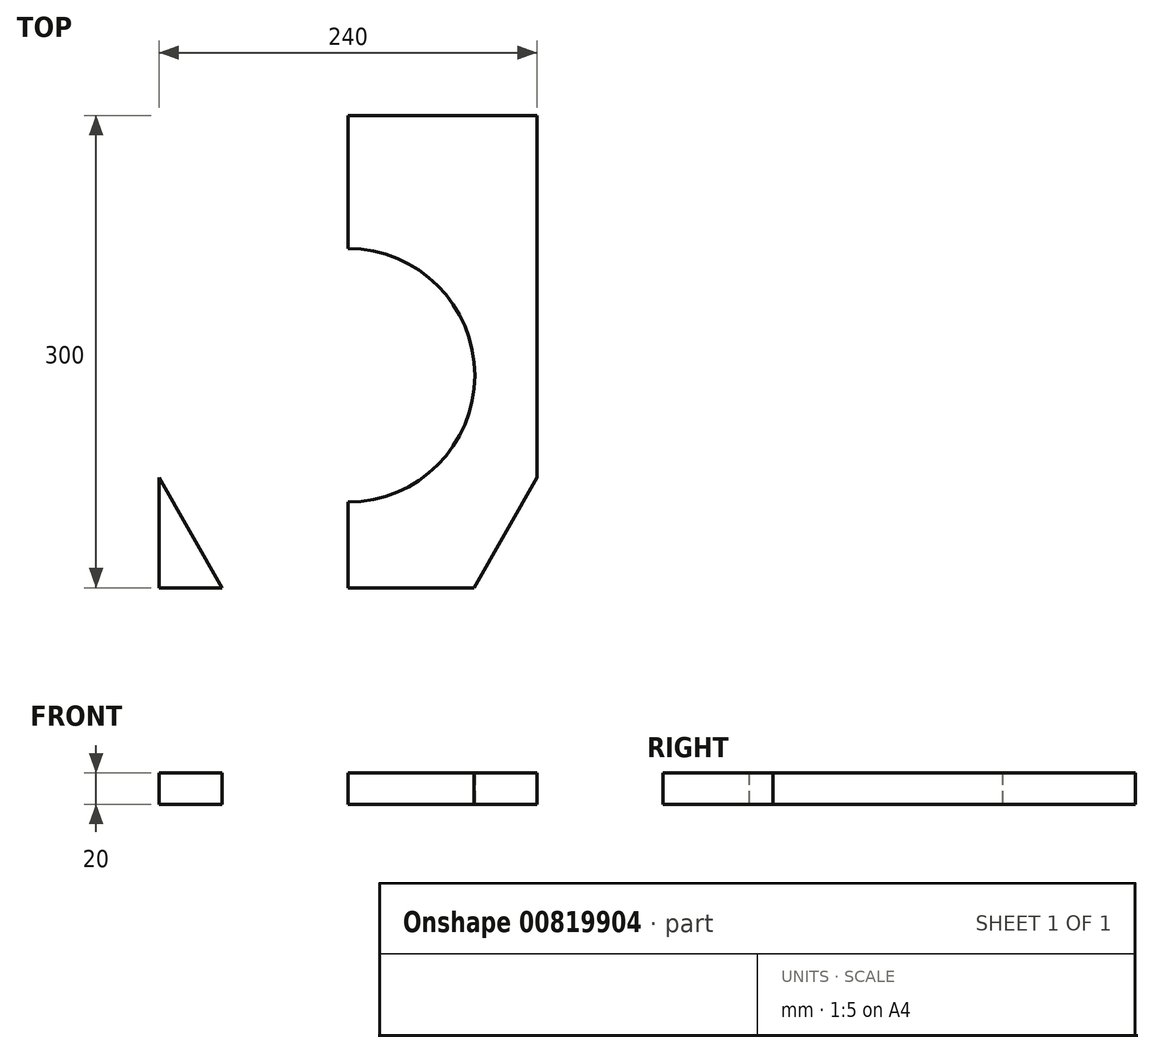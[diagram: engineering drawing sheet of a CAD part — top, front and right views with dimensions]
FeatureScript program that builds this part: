
annotation { "Feature Type Name" : "Feature", "Feature Type Description" : "" }
export const myFeature = defineFeature(function(context is Context, id is Id, definition is map)
    precondition{}
    {
        {
            var Q0;
            Q0=qCreatedBy(makeId("Top.planeOp"),FACE);
            var sketch = newSketch(context, id + "F0", { "sketchPlane" : qUnion([Q0])});
            skPoint(sketch, "E0.middle", {"position": v(0, 0) * mm});
            skLineSegment(sketch, "E1", {"start": v(-120, -30) * mm, "end": v(-120, -170) * mm});
            skLineSegment(sketch, "E2", {"start": v(-120, -170) * mm, "end": v(-120, -100) * mm});
            skLineSegment(sketch, "E3", {"start": v(-120, -170) * mm, "end": v(-80, -170) * mm});
            skLineSegment(sketch, "E4", {"start": v(-80, -170) * mm, "end": v(-120, -100) * mm});
            skLineSegment(sketch, "E5", {"start": v(-120, -30) * mm, "end": v(-120, 130) * mm});
            skLineSegment(sketch, "E6", {"start": v(-120, 130) * mm, "end": v(0, 130) * mm});
            skLineSegment(sketch, "E7", {"start": v(-120, -170) * mm, "end": v(0, -170) * mm});
            skLineSegment(sketch, "E8", {"start": v(0, -170) * mm, "end": v(0, 130) * mm});
            skLineSegment(sketch, "E9.MirrorCS", {"start": v(120, 130) * mm, "end": v(0, 130) * mm});
            skLineSegment(sketch, "E10.MirrorCS", {"start": v(120, -30) * mm, "end": v(120, 130) * mm});
            skLineSegment(sketch, "E11.MirrorCS", {"start": v(120, -30) * mm, "end": v(120, -170) * mm});
            skLineSegment(sketch, "E12.MirrorCS", {"start": v(80, -170) * mm, "end": v(120, -100) * mm});
            skLineSegment(sketch, "E13.MirrorCS", {"start": v(120, -170) * mm, "end": v(0, -170) * mm});
            skLineSegment(sketch, "E14", {"start": v(0, -170) * mm, "end": v(0, -35) * mm});
            skCircle(sketch, "E15", {"center": v(0, -35) * mm, "radius": 80.5 * mm});
            skSolve(sketch);
        }
        {
            var Q0;
            Q0=makeQuery(id+"F0.imprint","IMPRINT",FACE,{"disambiguationData":[TD([[makeQuery(id+"F0.imprint","IMPRINT",EDGE,{"derivedFrom":sQuery(id+"F0.wireOp",EDGE,"E1")}),1.0]])]});
            var Q1;
            {var subQ3=sQuery(id+"F0.wireOp",EDGE,"E9.MirrorCS");Q1=makeQuery(id+"F0.imprint","IMPRINT",FACE,{"disambiguationData":[TD([[makeQuery(id+"F0.imprint","IMPRINT",EDGE,{"derivedFrom":subQ3}),1.0]])]});}
            extrude(context, id + "F1", {"entities" : qUnion([Q0, Q1]), "depth" : 20 * mm, "offsetDistance" : 25 * mm});
        }
    });
